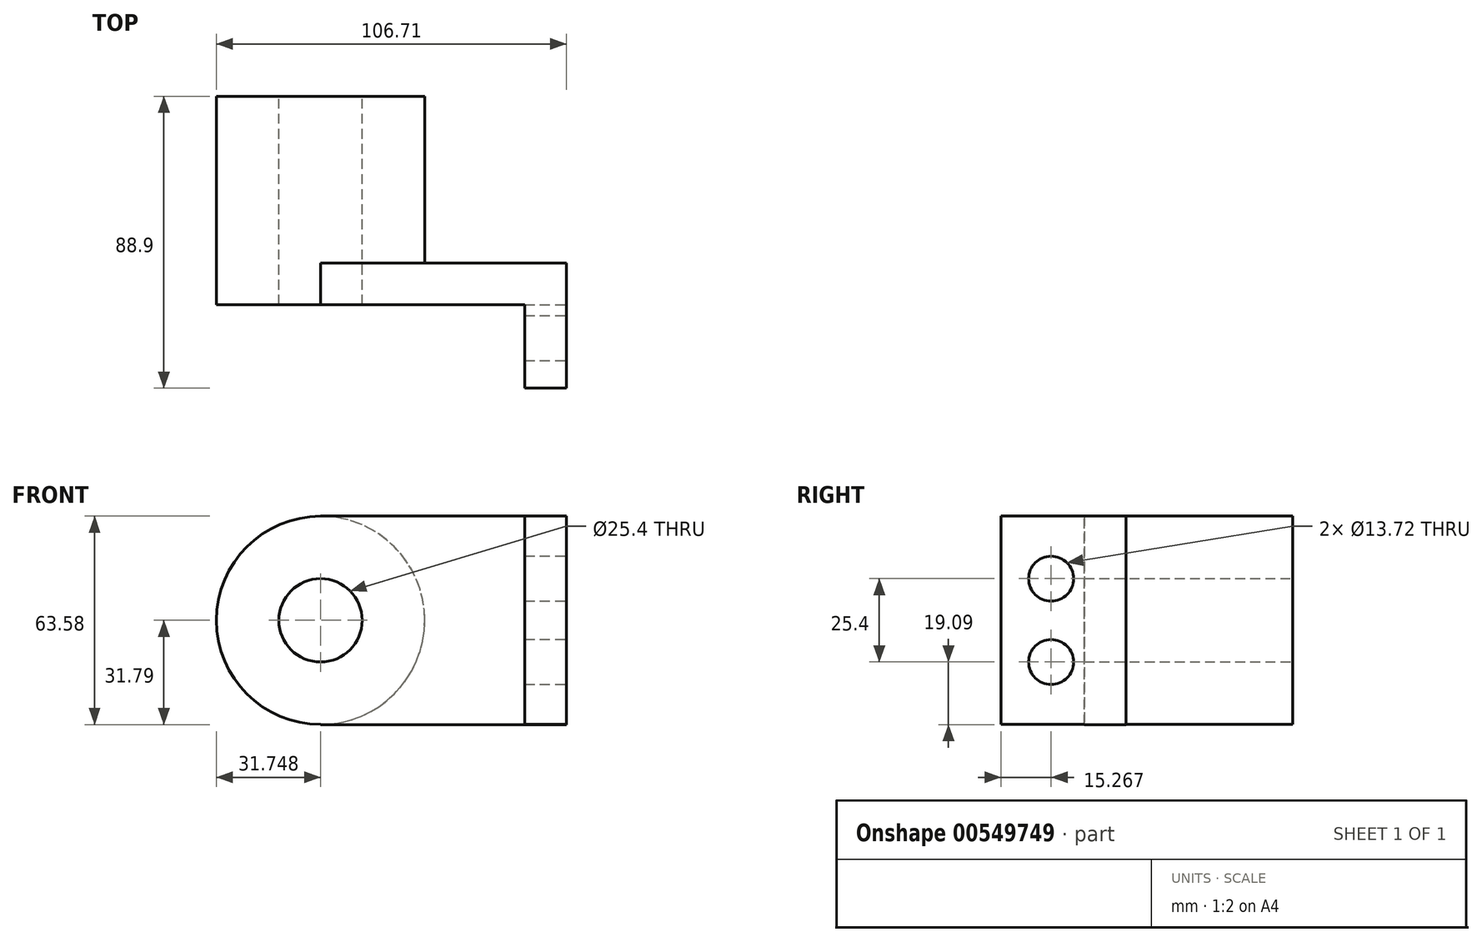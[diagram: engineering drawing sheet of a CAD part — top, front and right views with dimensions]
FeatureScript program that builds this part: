
annotation { "Feature Type Name" : "Feature", "Feature Type Description" : "" }
export const myFeature = defineFeature(function(context is Context, id is Id, definition is map)
    precondition{}
    {
        {
            var Q0;
            Q0=qCreatedBy(makeId("Front.planeOp"),FACE);
            var sketch = newSketch(context, id + "F0", { "sketchPlane" : qUnion([Q0])});
            skLineSegment(sketch, "E0.bottom", {"start": v(-37.48, -31.8) * mm, "end": v(37.48, -31.8) * mm});
            skLineSegment(sketch, "E0.top", {"start": v(-37.48, 31.8) * mm, "end": v(37.48, 31.8) * mm});
            skLineSegment(sketch, "E0.left", {"start": v(-37.48, -31.8) * mm, "end": v(-37.48, 31.8) * mm});
            skLineSegment(sketch, "E0.right", {"start": v(37.48, -31.8) * mm, "end": v(37.48, 31.8) * mm});
            skPoint(sketch, "E0.middle", {"position": v(0, 0) * mm});
            skCircle(sketch, "E1", {"center": v(-37.48, 0) * mm, "radius": 31.75 * mm});
            skCircle(sketch, "E2", {"center": v(-37.48, 0) * mm, "radius": 12.7 * mm});
            skSolve(sketch);
        }
        {
            var Q0;
            {var subQ0=sQuery(id+"F0.wireOp",EDGE,"E1");var subQ1=sQuery(id+"F0.wireOp",EDGE,"E0.left");var subQ2=makeQuery(id+"F0.imprint","INTERSECT",VERTEX,{"disambiguationData":[OD(0.0)],"derivedFrom":[subQ1,subQ0]});Q0=makeQuery(id+"F0.imprint","IMPRINT",FACE,{"disambiguationData":[TD([[makeQuery(id+"F0.imprint","IMPRINT",EDGE,{"disambiguationData":[TD([[subQ2,-1.0]])],"derivedFrom":subQ1}),1.0]])]});}
            var Q1;
            {var subQ0=sQuery(id+"F0.wireOp",EDGE,"E1");var subQ1=sQuery(id+"F0.wireOp",EDGE,"E0.left");var subQ2=makeQuery(id+"F0.imprint","INTERSECT",VERTEX,{"disambiguationData":[OD(0.0)],"derivedFrom":[subQ1,subQ0]});Q1=makeQuery(id+"F0.imprint","IMPRINT",FACE,{"disambiguationData":[TD([[makeQuery(id+"F0.imprint","IMPRINT",EDGE,{"disambiguationData":[TD([[subQ2,-1.0]])],"derivedFrom":subQ1}),-1.0]])]});}
            var Q2;
            {var subQ1=sQuery(id+"F0.wireOp",EDGE,"E0.bottom");Q2=makeQuery(id+"F0.imprint","IMPRINT",FACE,{"disambiguationData":[TD([[makeQuery(id+"F0.imprint","IMPRINT",EDGE,{"derivedFrom":subQ1}),1.0]])]});}
            extrude(context, id + "F1", {"entities" : qUnion([Q0, Q1, Q2]), "depth" : 12.7 * mm, "offsetDistance" : 25.4 * mm});
        }
        {
            var Q0;
            {var subQ0=sQuery(id+"F0.wireOp",EDGE,"E1");var subQ1=sQuery(id+"F0.wireOp",EDGE,"E0.left");var subQ2=makeQuery(id+"F0.imprint","INTERSECT",VERTEX,{"disambiguationData":[OD(0.0)],"derivedFrom":[subQ1,subQ0]});Q0=makeQuery(id+"F0.imprint","IMPRINT",FACE,{"disambiguationData":[TD([[makeQuery(id+"F0.imprint","IMPRINT",EDGE,{"disambiguationData":[TD([[subQ2,-1.0]])],"derivedFrom":subQ1}),-1.0]])]});}
            var Q1;
            {var subQ0=sQuery(id+"F0.wireOp",EDGE,"E1");var subQ1=sQuery(id+"F0.wireOp",EDGE,"E0.left");var subQ2=makeQuery(id+"F0.imprint","INTERSECT",VERTEX,{"disambiguationData":[OD(0.0)],"derivedFrom":[subQ1,subQ0]});Q1=makeQuery(id+"F0.imprint","IMPRINT",FACE,{"disambiguationData":[TD([[makeQuery(id+"F0.imprint","IMPRINT",EDGE,{"disambiguationData":[TD([[subQ2,-1.0]])],"derivedFrom":subQ1}),1.0]])]});}
            extrude(context, id + "F2", {"entities" : qUnion([Q0, Q1]), "operationType" : NewBodyOperationType.ADD, "oppositeDirection" : true, "depth" : 50.8 * mm, "offsetDistance" : 25.4 * mm});
        }
        {
            var Q0;
            Q0=makeQuery(id+"F1.opExtrude","SWEPT_FACE",FACE,{"disambiguationData":[OSD([sQuery(id+"F0.wireOp",EDGE,"E0.right")])]});
            var sketch = newSketch(context, id + "F3", { "sketchPlane" : qUnion([Q0])});
            skLineSegment(sketch, "E3.bottom", {"start": v(0, 31.8) * mm, "end": v(-38.1, 31.8) * mm});
            skLineSegment(sketch, "E3.top", {"start": v(0, -31.75) * mm, "end": v(-38.1, -31.75) * mm});
            skLineSegment(sketch, "E3.left", {"start": v(0, 31.8) * mm, "end": v(0, -31.75) * mm});
            skLineSegment(sketch, "E3.right", {"start": v(-38.1, 31.8) * mm, "end": v(-38.1, -31.75) * mm});
            skCircle(sketch, "E4", {"center": v(-22.83, 12.7) * mm, "radius": 6.86 * mm});
            skLineSegment(sketch, "E5", {"start": v(-12.7, 0) * mm, "end": v(-38.1, 0) * mm, "construction": true});
            skCircle(sketch, "E6.MirrorC", {"center": v(-22.83, -12.7) * mm, "radius": 6.86 * mm});
            skSolve(sketch);
        }
        {
            var Q0;
            {var subQ0=sQuery(id+"F3.wireOp",EDGE,"E3.right");Q0=makeQuery(id+"F3.imprint","IMPRINT",FACE,{"disambiguationData":[TD([[makeQuery(id+"F3.imprint","IMPRINT",EDGE,{"derivedFrom":subQ0}),1.0]])]});}
            extrude(context, id + "F4", {"entities" : qUnion([Q0]), "operationType" : NewBodyOperationType.ADD, "oppositeDirection" : true, "depth" : 12.7 * mm, "offsetDistance" : 25.4 * mm});
        }
    });
